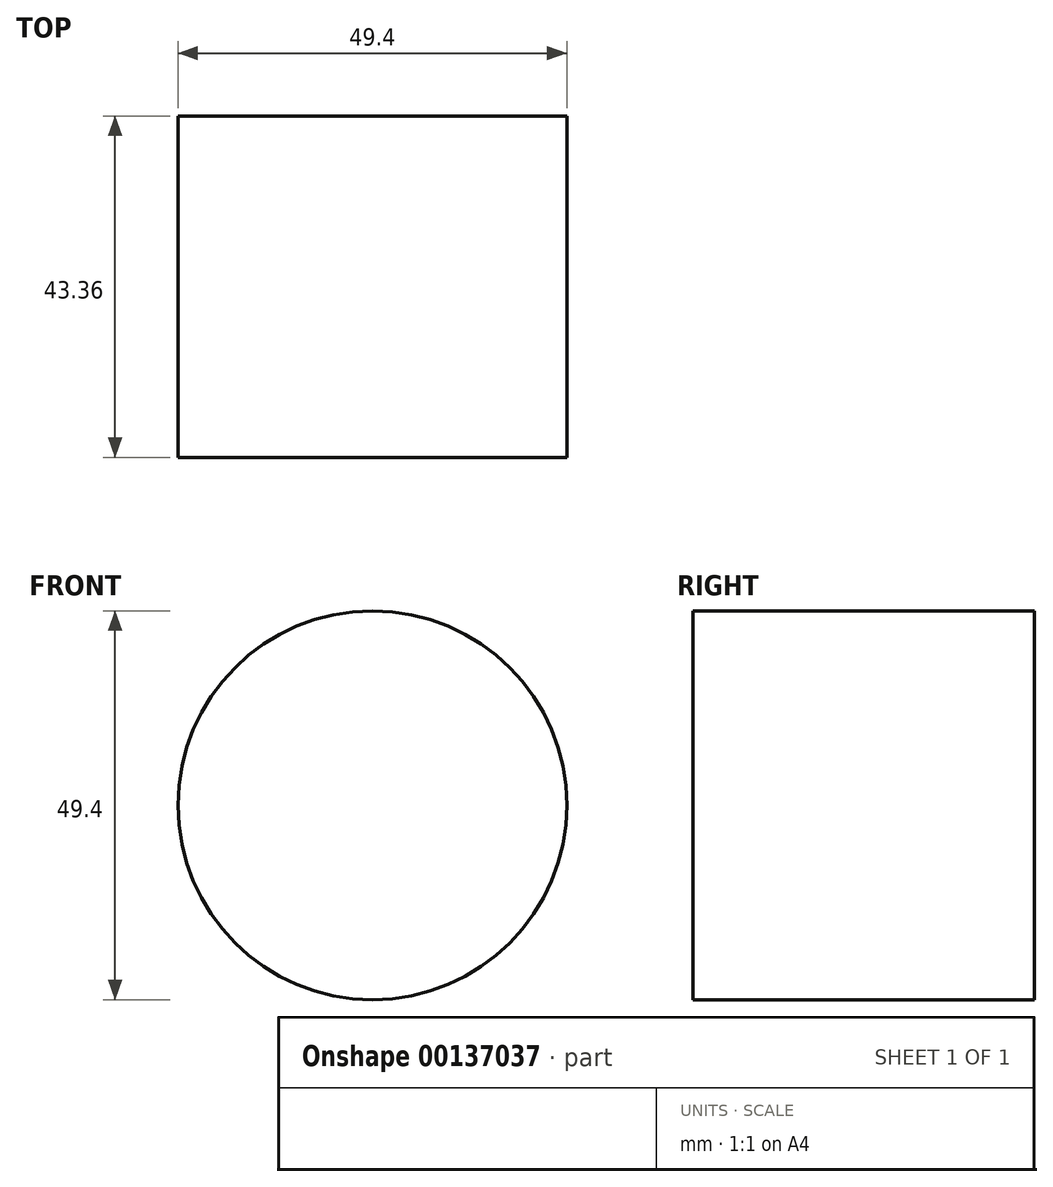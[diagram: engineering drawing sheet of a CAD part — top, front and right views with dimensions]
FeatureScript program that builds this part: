
annotation { "Feature Type Name" : "Feature", "Feature Type Description" : "" }
export const myFeature = defineFeature(function(context is Context, id is Id, definition is map)
    precondition{}
    {
        {
            var Q0;
            Q0=qCreatedBy(makeId("Front.planeOp"),FACE);
            var sketch = newSketch(context, id + "F0", { "sketchPlane" : qUnion([Q0])});
            skCircle(sketch, "E0", {"center": v(0, 0) * mm, "radius": 24.7 * mm});
            skSolve(sketch);
        }
        {
            var Q0;
            Q0 = qSketchRegion(id + "F0", true);
            var Q1;
            Q1=makeQuery(id+"F0.imprint","IMPRINT",FACE,{"disambiguationData":[TD([[makeQuery(id+"F0.imprint","IMPRINT",EDGE,{"derivedFrom":sQuery(id+"F0.wireOp",EDGE,"E0")}),1.0]])]});
            extrude(context, id + "F1", {"entities" : qUnion([Q0, Q1]), "depth" : 43.36 * mm});
        }
    });
